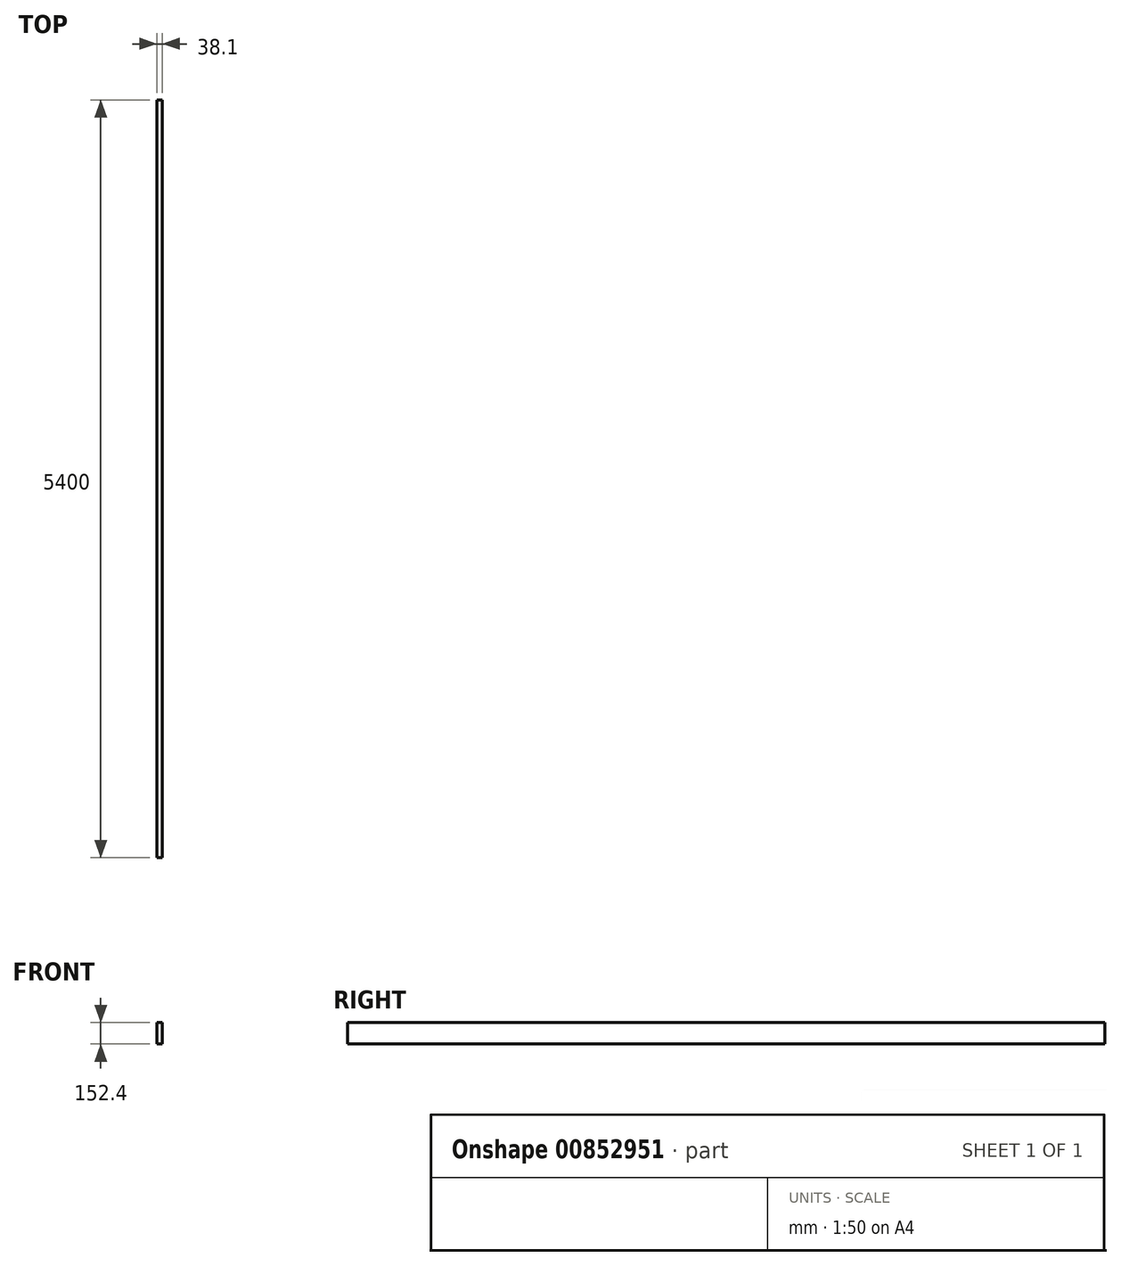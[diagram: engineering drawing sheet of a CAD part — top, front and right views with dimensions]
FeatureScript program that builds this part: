
annotation { "Feature Type Name" : "Feature", "Feature Type Description" : "" }
export const myFeature = defineFeature(function(context is Context, id is Id, definition is map)
    precondition{}
    {
        {
            var Q0;
            Q0=qCreatedBy(makeId("Front.planeOp"),FACE);
            var sketch = newSketch(context, id + "F0", { "sketchPlane" : qUnion([Q0])});
            skLineSegment(sketch, "E0.bottom", {"start": v(0, 0) * mm, "end": v(-38.1, 0) * mm});
            skLineSegment(sketch, "E0.top", {"start": v(0, 152.4) * mm, "end": v(-38.1, 152.4) * mm});
            skLineSegment(sketch, "E0.left", {"start": v(0, 0) * mm, "end": v(0, 152.4) * mm});
            skLineSegment(sketch, "E0.right", {"start": v(-38.1, 0) * mm, "end": v(-38.1, 152.4) * mm});
            skSolve(sketch);
        }
        {
            var Q0;
            Q0 = qSketchRegion(id + "F0", true);
            extrude(context, id + "F1", {"entities" : qUnion([Q0]), "depth" : 5400 * mm, "offsetDistance" : 25.4 * mm});
        }
    });
